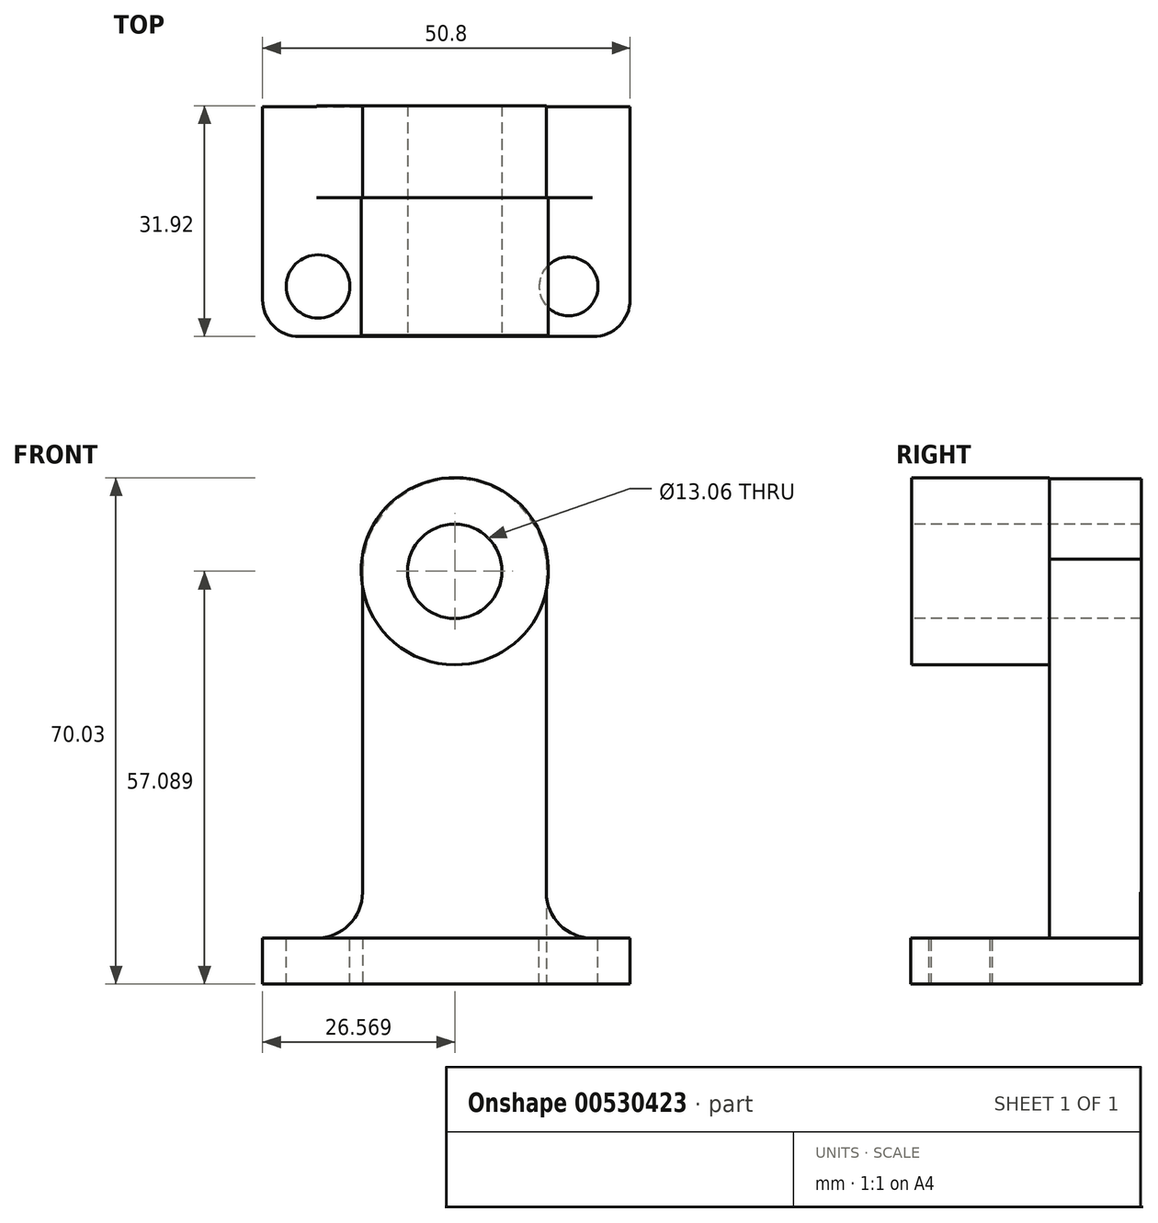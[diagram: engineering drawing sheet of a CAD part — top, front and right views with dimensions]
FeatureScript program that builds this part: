
annotation { "Feature Type Name" : "Feature", "Feature Type Description" : "" }
export const myFeature = defineFeature(function(context is Context, id is Id, definition is map)
    precondition{}
    {
        {
            var Q0;
            Q0=qCreatedBy(makeId("Front.planeOp"),FACE);
            var sketch = newSketch(context, id + "F0", { "sketchPlane" : qUnion([Q0])});
            skLineSegment(sketch, "E0", {"start": v(-46.82, 69.85) * mm, "end": v(-46.82, 0) * mm});
            skLineSegment(sketch, "E1", {"start": v(-46.82, 69.85) * mm, "end": v(-21.42, 69.85) * mm});
            skLineSegment(sketch, "E2", {"start": v(-21.42, 69.85) * mm, "end": v(-21.42, 0) * mm});
            skLineSegment(sketch, "E3", {"start": v(-46.82, 0) * mm, "end": v(-21.42, 0) * mm});
            skSolve(sketch);
        }
        {
            var Q0;
            Q0 = qSketchRegion(id + "F0", true);
            extrude(context, id + "F1", {"entities" : qUnion([Q0]), "depth" : 12.7 * mm, "offsetDistance" : 25.4 * mm});
        }
        {
            var Q0;
            Q0=makeQuery(id+"F1.opExtrude","CAP_FACE",FACE,{"disambiguationData":[OSD([sQuery(id+"F0.wireOp",EDGE,"E0"),sQuery(id+"F0.wireOp",EDGE,"E1"),sQuery(id+"F0.wireOp",EDGE,"E2"),sQuery(id+"F0.wireOp",EDGE,"E3")])],"isStart":false});
            var sketch = newSketch(context, id + "F2", { "sketchPlane" : qUnion([Q0])});
            skArc(sketch, "E4", {"start": v(-21.42, 55.38) * mm, "mid": v(-33.17, 69.82) * mm, "end": v(-46.82, 57.16) * mm});
            skSolve(sketch);
        }
        {
            var Q0;
            {var subQ5=makeQuery(id+"F1.opExtrude","CAP_EDGE",EDGE,{"disambiguationData":[OSD([sQuery(id+"F0.wireOp",EDGE,"E1")])],"isStart":false});Q0=makeQuery(id+"F2.imprint","IMPRINT",FACE,{"disambiguationData":[TD([[makeQuery(id+"F2.imprint","IMPRINT",EDGE,{"derivedFrom":subQ5}),-1.0]])]});}
            extrude(context, id + "F3", {"entities" : qUnion([Q0]), "operationType" : NewBodyOperationType.REMOVE, "endBound" : BoundingType.THROUGH_ALL, "oppositeDirection" : true, "depth" : 25.4 * mm, "offsetDistance" : 25.4 * mm});
        }
        {
            var Q0;
            Q0=makeQuery(id+"F1.opExtrude","CAP_FACE",FACE,{"disambiguationData":[OSD([sQuery(id+"F0.wireOp",EDGE,"E0"),sQuery(id+"F0.wireOp",EDGE,"E1"),sQuery(id+"F0.wireOp",EDGE,"E2"),sQuery(id+"F0.wireOp",EDGE,"E3")])],"isStart":false});
            var sketch = newSketch(context, id + "F4", { "sketchPlane" : qUnion([Q0])});
            skCircle(sketch, "E5", {"center": v(-34.06, 57.09) * mm, "radius": 12.94 * mm});
            skSolve(sketch);
        }
        {
            var Q0;
            Q0=makeQuery(id+"F4.imprint","IMPRINT",FACE,{"disambiguationData":[TD([[makeQuery(id+"F4.imprint","IMPRINT",EDGE,{"derivedFrom":sQuery(id+"F4.wireOp",EDGE,"E5")}),1.0]])]});
            extrude(context, id + "F5", {"entities" : qUnion([Q0]), "operationType" : NewBodyOperationType.ADD, "depth" : 19.05 * mm, "offsetDistance" : 25.4 * mm});
        }
        {
            var Q0;
            Q0=makeQuery(id+"F5.opExtrude","CAP_FACE",FACE,{"disambiguationData":[OSD([sQuery(id+"F4.wireOp",EDGE,"E5")])],"isStart":false});
            var sketch = newSketch(context, id + "F6", { "sketchPlane" : qUnion([Q0])});
            skCircle(sketch, "E6", {"center": v(-34.06, 57.09) * mm, "radius": 6.53 * mm});
            skSolve(sketch);
        }
        {
            var Q0;
            Q0=makeQuery(id+"F6.imprint","IMPRINT",FACE,{"disambiguationData":[TD([[makeQuery(id+"F6.imprint","IMPRINT",EDGE,{"derivedFrom":sQuery(id+"F6.wireOp",EDGE,"E6")}),1.0]])]});
            extrude(context, id + "F7", {"entities" : qUnion([Q0]), "operationType" : NewBodyOperationType.REMOVE, "endBound" : BoundingType.THROUGH_ALL, "oppositeDirection" : true, "depth" : 25.4 * mm, "offsetDistance" : 25.4 * mm});
        }
        {
            var Q0;
            Q0=qCreatedBy(makeId("Top.planeOp"),FACE);
            var sketch = newSketch(context, id + "F8", { "sketchPlane" : qUnion([Q0])});
            skLineSegment(sketch, "E7.bottom", {"start": v(-60.63, -0.17) * mm, "end": v(-9.83, -0.17) * mm});
            skLineSegment(sketch, "E7.top", {"start": v(-60.63, -31.92) * mm, "end": v(-9.83, -31.92) * mm});
            skLineSegment(sketch, "E7.left", {"start": v(-60.63, -0.17) * mm, "end": v(-60.63, -31.92) * mm});
            skLineSegment(sketch, "E7.right", {"start": v(-9.83, -0.17) * mm, "end": v(-9.83, -31.92) * mm});
            skSolve(sketch);
        }
        {
            var Q0;
            Q0=makeQuery(id+"F8.imprint","IMPRINT",FACE,{"disambiguationData":[TD([[makeQuery(id+"F8.imprint","IMPRINT",EDGE,{"derivedFrom":sQuery(id+"F8.wireOp",EDGE,"E7.bottom")}),-1.0]])]});
            extrude(context, id + "F9", {"entities" : qUnion([Q0]), "operationType" : NewBodyOperationType.ADD, "depth" : 6.35 * mm, "offsetDistance" : 25.4 * mm});
        }
        {
            var Q0;
            Q0=makeQuery(id+"F9.opExtrude","CAP_FACE",FACE,{"disambiguationData":[OSD([sQuery(id+"F8.wireOp",EDGE,"E7.bottom"),sQuery(id+"F8.wireOp",EDGE,"E7.top"),sQuery(id+"F8.wireOp",EDGE,"E7.left"),sQuery(id+"F8.wireOp",EDGE,"E7.right")])],"isStart":false});
            var sketch = newSketch(context, id + "F10", { "sketchPlane" : qUnion([Q0])});
            skCircle(sketch, "E8", {"center": v(-18.33, -24.99) * mm, "radius": 4.06 * mm});
            skCircle(sketch, "E9", {"center": v(-52.95, -24.99) * mm, "radius": 4.38 * mm});
            skSolve(sketch);
        }
        {
            var Q0;
            Q0=makeQuery(id+"F10.imprint","IMPRINT",FACE,{"disambiguationData":[TD([[makeQuery(id+"F10.imprint","IMPRINT",EDGE,{"derivedFrom":sQuery(id+"F10.wireOp",EDGE,"fPW7hecr-RpFH-Evfj-kExd-6QSjVOmFYihe")}),1.0]])]});
            var Q1;
            Q1=makeQuery(id+"F10.imprint","IMPRINT",FACE,{"disambiguationData":[TD([[makeQuery(id+"F10.imprint","IMPRINT",EDGE,{"derivedFrom":sQuery(id+"F10.wireOp",EDGE,"HLfQN0Yi-punc-iS16-G6WA-ixTniyIDgVXK")}),1.0]])]});
            var Q2;
            Q2=makeQuery(id+"F10.imprint","IMPRINT",FACE,{"disambiguationData":[TD([[makeQuery(id+"F10.imprint","IMPRINT",EDGE,{"derivedFrom":sQuery(id+"F10.wireOp",EDGE,"E9")}),1.0]])]});
            var Q3;
            Q3=makeQuery(id+"F10.imprint","IMPRINT",FACE,{"disambiguationData":[TD([[makeQuery(id+"F10.imprint","IMPRINT",EDGE,{"derivedFrom":sQuery(id+"F10.wireOp",EDGE,"E8")}),1.0]])]});
            extrude(context, id + "F11", {"entities" : qUnion([Q0, Q1, Q2, Q3]), "operationType" : NewBodyOperationType.REMOVE, "oppositeDirection" : true, "depth" : 25.4 * mm, "offsetDistance" : 25.4 * mm});
        }
        {
            var Q0;
            Q0=qCreatedBy(makeId("Front.planeOp"),FACE);
            var sketch = newSketch(context, id + "F12", { "sketchPlane" : qUnion([Q0])});
            skLineSegment(sketch, "E10.bottom", {"start": v(-47.13, 19.55) * mm, "end": v(-59.83, 19.55) * mm});
            skLineSegment(sketch, "E10.top", {"start": v(-47.13, 6.85) * mm, "end": v(-59.83, 6.85) * mm});
            skLineSegment(sketch, "E10.left", {"start": v(-47.13, 19.55) * mm, "end": v(-47.13, 6.85) * mm});
            skLineSegment(sketch, "E10.right", {"start": v(-59.83, 19.55) * mm, "end": v(-59.83, 6.85) * mm});
            skLineSegment(sketch, "E11.bottom", {"start": v(-21.07, 19.06) * mm, "end": v(-8.37, 19.06) * mm});
            skLineSegment(sketch, "E11.top", {"start": v(-21.07, 6.36) * mm, "end": v(-8.37, 6.36) * mm});
            skLineSegment(sketch, "E11.left", {"start": v(-21.07, 19.06) * mm, "end": v(-21.07, 6.36) * mm});
            skLineSegment(sketch, "E11.right", {"start": v(-8.37, 19.06) * mm, "end": v(-8.37, 6.36) * mm});
            skCircle(sketch, "E12", {"center": v(-53.48, 13.2) * mm, "radius": 6.35 * mm});
            skCircle(sketch, "E13", {"center": v(-14.9, 12.53) * mm, "radius": 6.17 * mm});
            skSolve(sketch);
        }
        {
            var Q0;
            {var subQ0=sQuery(id+"F12.wireOp",EDGE,"E12");var subQ1=makeQuery(id+"F12.imprint","INTERSECT",VERTEX,{"derivedFrom":[sQuery(id+"F12.wireOp",EDGE,"E10.bottom"),subQ0]});Q0=makeQuery(id+"F12.imprint","IMPRINT",FACE,{"disambiguationData":[TD([[makeQuery(id+"F12.imprint","IMPRINT",EDGE,{"disambiguationData":[TD([[subQ1,1.0]])],"derivedFrom":subQ0}),1.0]])]});}
            var Q1;
            {var subQ0=sQuery(id+"F12.wireOp",EDGE,"E10.right");var subQ1=sQuery(id+"F12.wireOp",EDGE,"E10.bottom");var subQ2=makeQuery(id+"F12.imprint","INTERSECT",VERTEX,{"derivedFrom":[subQ1,subQ0]});Q1=makeQuery(id+"F12.imprint","IMPRINT",FACE,{"disambiguationData":[TD([[makeQuery(id+"F12.imprint","IMPRINT",EDGE,{"disambiguationData":[TD([[subQ2,1.0]])],"derivedFrom":subQ1}),1.0]])]});}
            var Q2;
            {var subQ0=sQuery(id+"F12.wireOp",EDGE,"E10.right");var subQ1=sQuery(id+"F12.wireOp",EDGE,"E10.top");var subQ2=makeQuery(id+"F12.imprint","INTERSECT",VERTEX,{"derivedFrom":[subQ1,subQ0]});Q2=makeQuery(id+"F12.imprint","IMPRINT",FACE,{"disambiguationData":[TD([[makeQuery(id+"F12.imprint","IMPRINT",EDGE,{"disambiguationData":[TD([[subQ2,1.0]])],"derivedFrom":subQ1}),-1.0]])]});}
            var Q3;
            {var subQ0=sQuery(id+"F12.wireOp",EDGE,"E10.left");var subQ1=sQuery(id+"F12.wireOp",EDGE,"E10.bottom");var subQ2=makeQuery(id+"F12.imprint","INTERSECT",VERTEX,{"derivedFrom":[subQ1,subQ0]});Q3=makeQuery(id+"F12.imprint","IMPRINT",FACE,{"disambiguationData":[TD([[makeQuery(id+"F12.imprint","IMPRINT",EDGE,{"disambiguationData":[TD([[subQ2,-1.0]])],"derivedFrom":subQ1}),1.0]])]});}
            var Q4;
            {var subQ0=sQuery(id+"F12.wireOp",EDGE,"E13");var subQ1=makeQuery(id+"F12.imprint","INTERSECT",VERTEX,{"derivedFrom":[sQuery(id+"F12.wireOp",EDGE,"E11.top"),subQ0]});Q4=makeQuery(id+"F12.imprint","IMPRINT",FACE,{"disambiguationData":[TD([[makeQuery(id+"F12.imprint","IMPRINT",EDGE,{"disambiguationData":[TD([[subQ1,1.0]])],"derivedFrom":subQ0}),1.0]])]});}
            extrude(context, id + "F13", {"entities" : qUnion([Q0, Q1, Q2, Q3, Q4]), "operationType" : NewBodyOperationType.REMOVE, "endBound" : BoundingType.THROUGH_ALL, "oppositeDirection" : true, "depth" : 25.4 * mm, "offsetDistance" : 25.4 * mm});
        }
        {
            var Q0;
            Q0=makeQuery(id+"F9.opExtrude","SWEPT_EDGE",EDGE,{"disambiguationData":[OSD([sQuery(id+"F8.wireOp",EDGE,"E7.top"),sQuery(id+"F8.wireOp",EDGE,"E7.right")])]});
            var Q1;
            Q1=makeQuery(id+"F9.opExtrude","SWEPT_EDGE",EDGE,{"disambiguationData":[OSD([sQuery(id+"F8.wireOp",EDGE,"E7.top"),sQuery(id+"F8.wireOp",EDGE,"E7.left")])]});
            fillet(context, id + "F14", {"entities" : qUnion([Q0, Q1]), "radius" : 5.08 * mm, "tangentPropagation" : true, "allowEdgeOverflow" : false});
        }
        {
            var Q0;
            Q0=makeQuery(id+"F1.opExtrude","SWEPT_FACE",FACE,{"disambiguationData":[OSD([sQuery(id+"F0.wireOp",EDGE,"E2")])]});
            var sketch = newSketch(context, id + "F15", { "sketchPlane" : qUnion([Q0])});
            skLineSegment(sketch, "E14.bottom", {"start": v(-12.7, 15.74) * mm, "end": v(-0.17, 15.74) * mm});
            skLineSegment(sketch, "E14.top", {"start": v(-12.7, 6.35) * mm, "end": v(-0.17, 6.35) * mm});
            skLineSegment(sketch, "E14.left", {"start": v(-12.7, 15.74) * mm, "end": v(-12.7, 6.35) * mm});
            skLineSegment(sketch, "E14.right", {"start": v(-0.17, 15.74) * mm, "end": v(-0.17, 6.35) * mm});
            skSolve(sketch);
        }
        {
            var Q0;
            Q0=makeQuery(id+"F15.imprint","IMPRINT",FACE,{"disambiguationData":[TD([[makeQuery(id+"F15.imprint","IMPRINT",EDGE,{"derivedFrom":sQuery(id+"F15.wireOp",EDGE,"E14.bottom")}),-1.0]])]});
            extrude(context, id + "F16", {"entities" : qUnion([Q0]), "operationType" : NewBodyOperationType.ADD, "depth" : 12.7 * mm, "offsetDistance" : 25.4 * mm});
        }
        {
            var Q0;
            Q0=makeQuery(id+"F16.boolean.opBoolean","MERGE",FACE,{"derivedFrom":[makeQuery(id+"F1.opExtrude","CAP_FACE",FACE,{"disambiguationData":[OSD([sQuery(id+"F0.wireOp",EDGE,"E0"),sQuery(id+"F0.wireOp",EDGE,"E1"),sQuery(id+"F0.wireOp",EDGE,"E2"),sQuery(id+"F0.wireOp",EDGE,"E3")])],"isStart":false}),makeQuery(id+"F16.opExtrude","SWEPT_FACE",FACE,{"disambiguationData":[OSD([sQuery(id+"F15.wireOp",EDGE,"E14.left")])]})]});
            var sketch = newSketch(context, id + "F17", { "sketchPlane" : qUnion([Q0])});
            skLineSegment(sketch, "E15", {"start": v(-21.42, 15.74) * mm, "end": v(-21.42, 6.35) * mm});
            skLineSegment(sketch, "E16", {"start": v(-8.72, 15.74) * mm, "end": v(-8.72, 6.35) * mm});
            skCircle(sketch, "E17", {"center": v(-15.07, 12.7) * mm, "radius": 6.35 * mm});
            skSolve(sketch);
        }
        {
            var Q0;
            {var subQ0=sQuery(id+"F17.wireOp",EDGE,"E17");var subQ1=makeQuery(id+"F17.imprint","INTERSECT",VERTEX,{"derivedFrom":[sQuery(id+"F17.wireOp",EDGE,"E16"),subQ0]});Q0=makeQuery(id+"F17.imprint","IMPRINT",FACE,{"disambiguationData":[TD([[makeQuery(id+"F17.imprint","IMPRINT",EDGE,{"disambiguationData":[TD([[subQ1,-1.0]])],"derivedFrom":subQ0}),1.0]])]});}
            var Q1;
            {var subQ0=sQuery(id+"F17.wireOp",EDGE,"E17");var subQ1=makeQuery(id+"F16.opExtrude","SWEPT_EDGE",EDGE,{"disambiguationData":[OSD([sQuery(id+"F0.wireOp",EDGE,"E2"),sQuery(id+"F15.wireOp",EDGE,"E14.bottom"),sQuery(id+"F15.wireOp",EDGE,"E14.left")])]});var subQ2=makeQuery(id+"F17.imprint","INTERSECT",VERTEX,{"disambiguationData":[OD(0.0)],"derivedFrom":[subQ1,subQ0]});Q1=makeQuery(id+"F17.imprint","IMPRINT",FACE,{"disambiguationData":[TD([[makeQuery(id+"F17.imprint","IMPRINT",EDGE,{"disambiguationData":[TD([[subQ2,-1.0]])],"derivedFrom":subQ0}),1.0]])]});}
            var Q2;
            {var subQ1=makeQuery(id+"F16.opExtrude","SWEPT_EDGE",EDGE,{"disambiguationData":[OSD([sQuery(id+"F15.wireOp",EDGE,"E14.top"),sQuery(id+"F15.wireOp",EDGE,"E14.left")])]});var subQ2=makeQuery(id+"F16.boolean.opBoolean","SPLIT",EDGE,{"derivedFrom":subQ1});Q2=makeQuery(id+"F17.imprint","IMPRINT",FACE,{"disambiguationData":[TD([[makeQuery(id+"F17.imprint","IMPRINT",EDGE,{"derivedFrom":subQ2}),-1.0]])]});}
            var Q3;
            {var subQ0=sQuery(id+"F17.wireOp",EDGE,"E16");var subQ3=sQuery(id+"F17.wireOp",EDGE,"E17");var subQ4=makeQuery(id+"F17.imprint","INTERSECT",VERTEX,{"derivedFrom":[subQ0,subQ3]});Q3=makeQuery(id+"F17.imprint","IMPRINT",FACE,{"disambiguationData":[TD([[makeQuery(id+"F17.imprint","IMPRINT",EDGE,{"disambiguationData":[TD([[subQ4,1.0]])],"derivedFrom":subQ0}),-1.0]])]});}
            extrude(context, id + "F18", {"entities" : qUnion([Q0, Q1, Q2, Q3]), "operationType" : NewBodyOperationType.REMOVE, "oppositeDirection" : true, "depth" : 25.4 * mm, "offsetDistance" : 25.4 * mm});
        }
        {
            var Q0;
            Q0=makeQuery(id+"F1.opExtrude","SWEPT_FACE",FACE,{"disambiguationData":[OSD([sQuery(id+"F0.wireOp",EDGE,"E0")])]});
            var sketch = newSketch(context, id + "F19", { "sketchPlane" : qUnion([Q0])});
            skLineSegment(sketch, "E18.bottom", {"start": v(0, 16.45) * mm, "end": v(12.7, 16.45) * mm});
            skLineSegment(sketch, "E18.top", {"start": v(0, 6.35) * mm, "end": v(12.7, 6.35) * mm});
            skLineSegment(sketch, "E18.left", {"start": v(0, 16.45) * mm, "end": v(0, 6.35) * mm});
            skLineSegment(sketch, "E18.right", {"start": v(12.7, 16.45) * mm, "end": v(12.7, 6.35) * mm});
            skSolve(sketch);
        }
        {
            var Q0;
            Q0=makeQuery(id+"F19.imprint","IMPRINT",FACE,{"disambiguationData":[TD([[makeQuery(id+"F19.imprint","IMPRINT",EDGE,{"derivedFrom":sQuery(id+"F19.wireOp",EDGE,"E18.bottom")}),-1.0]])]});
            extrude(context, id + "F20", {"entities" : qUnion([Q0]), "operationType" : NewBodyOperationType.ADD, "depth" : 12.7 * mm, "offsetDistance" : 25.4 * mm});
        }
        {
            var Q0;
            Q0=makeQuery(id+"F20.boolean.opBoolean","MERGE",FACE,{"derivedFrom":[makeQuery(id+"F16.boolean.opBoolean","MERGE",FACE,{"derivedFrom":[makeQuery(id+"F1.opExtrude","CAP_FACE",FACE,{"disambiguationData":[OSD([sQuery(id+"F0.wireOp",EDGE,"E0"),sQuery(id+"F0.wireOp",EDGE,"E1"),sQuery(id+"F0.wireOp",EDGE,"E2"),sQuery(id+"F0.wireOp",EDGE,"E3")])],"isStart":false}),makeQuery(id+"F16.opExtrude","SWEPT_FACE",FACE,{"disambiguationData":[OSD([sQuery(id+"F15.wireOp",EDGE,"E14.left")])]})]}),makeQuery(id+"F20.opExtrude","SWEPT_FACE",FACE,{"disambiguationData":[OSD([sQuery(id+"F19.wireOp",EDGE,"E18.right")])]})]});
            var sketch = newSketch(context, id + "F21", { "sketchPlane" : qUnion([Q0])});
            skLineSegment(sketch, "E19", {"start": v(-46.82, 16.45) * mm, "end": v(-46.82, 6.35) * mm});
            skLineSegment(sketch, "E20", {"start": v(-21.42, 26.05) * mm, "end": v(-21.42, 6.35) * mm});
            skCircle(sketch, "E21", {"center": v(-53.17, 12.7) * mm, "radius": 6.35 * mm});
            skSolve(sketch);
        }
        {
            var Q0;
            {var subQ0=sQuery(id+"F21.wireOp",EDGE,"E21");var subQ1=sQuery(id+"F19.wireOp",EDGE,"E18.right");var subQ2=makeQuery(id+"F20.opExtrude","CAP_EDGE",EDGE,{"disambiguationData":[OSD([subQ1])],"isStart":false});var subQ3=makeQuery(id+"F21.imprint","INTERSECT",VERTEX,{"derivedFrom":[subQ2,subQ0]});Q0=makeQuery(id+"F21.imprint","IMPRINT",FACE,{"disambiguationData":[TD([[makeQuery(id+"F21.imprint","IMPRINT",EDGE,{"disambiguationData":[TD([[subQ3,-1.0]])],"derivedFrom":subQ0}),-1.0]])]});}
            var Q1;
            {var subQ1=makeQuery(id+"F16.opExtrude","SWEPT_EDGE",EDGE,{"disambiguationData":[OSD([sQuery(id+"F0.wireOp",EDGE,"E2"),sQuery(id+"F15.wireOp",EDGE,"E14.bottom"),sQuery(id+"F15.wireOp",EDGE,"E14.left")])]});Q1=makeQuery(id+"F21.imprint","IMPRINT",FACE,{"disambiguationData":[TD([[makeQuery(id+"F21.imprint","IMPRINT",EDGE,{"derivedFrom":subQ1}),1.0]])]});}
            var Q2;
            {var subQ0=sQuery(id+"F21.wireOp",EDGE,"E21");var subQ1=sQuery(id+"F19.wireOp",EDGE,"E18.right");var subQ4=makeQuery(id+"F20.opExtrude","CAP_EDGE",EDGE,{"disambiguationData":[OSD([subQ1])],"isStart":false});var subQ5=makeQuery(id+"F21.imprint","INTERSECT",VERTEX,{"derivedFrom":[subQ4,subQ0]});Q2=makeQuery(id+"F21.imprint","IMPRINT",FACE,{"disambiguationData":[TD([[makeQuery(id+"F21.imprint","IMPRINT",EDGE,{"disambiguationData":[TD([[subQ5,1.0]])],"derivedFrom":subQ0}),-1.0]])]});}
            var Q3;
            {var subQ0=sQuery(id+"F21.wireOp",EDGE,"E21");var subQ1=makeQuery(id+"F20.opExtrude","SWEPT_EDGE",EDGE,{"disambiguationData":[OSD([sQuery(id+"F0.wireOp",EDGE,"E0"),sQuery(id+"F19.wireOp",EDGE,"E18.bottom"),sQuery(id+"F19.wireOp",EDGE,"E18.right")])]});var subQ2=makeQuery(id+"F21.imprint","INTERSECT",VERTEX,{"disambiguationData":[OD(0.0)],"derivedFrom":[subQ1,subQ0]});Q3=makeQuery(id+"F21.imprint","IMPRINT",FACE,{"disambiguationData":[TD([[makeQuery(id+"F21.imprint","IMPRINT",EDGE,{"disambiguationData":[TD([[subQ2,-1.0]])],"derivedFrom":subQ0}),1.0]])]});}
            var Q4;
            {var subQ0=sQuery(id+"F21.wireOp",EDGE,"E21");var subQ1=makeQuery(id+"F21.imprint","INTERSECT",VERTEX,{"derivedFrom":[sQuery(id+"F21.wireOp",EDGE,"E19"),subQ0]});Q4=makeQuery(id+"F21.imprint","IMPRINT",FACE,{"disambiguationData":[TD([[makeQuery(id+"F21.imprint","IMPRINT",EDGE,{"disambiguationData":[TD([[subQ1,-1.0]])],"derivedFrom":subQ0}),1.0]])]});}
            extrude(context, id + "F22", {"entities" : qUnion([Q0, Q1, Q2, Q3, Q4]), "operationType" : NewBodyOperationType.REMOVE, "oppositeDirection" : true, "depth" : 25.4 * mm, "offsetDistance" : 25.4 * mm});
        }
        {
            var Q0;
            Q0=makeQuery(id+"F20.boolean.opBoolean","MERGE",FACE,{"derivedFrom":[makeQuery(id+"F16.boolean.opBoolean","MERGE",FACE,{"derivedFrom":[makeQuery(id+"F1.opExtrude","CAP_FACE",FACE,{"disambiguationData":[OSD([sQuery(id+"F0.wireOp",EDGE,"E0"),sQuery(id+"F0.wireOp",EDGE,"E1"),sQuery(id+"F0.wireOp",EDGE,"E2"),sQuery(id+"F0.wireOp",EDGE,"E3")])],"isStart":false}),makeQuery(id+"F16.opExtrude","SWEPT_FACE",FACE,{"disambiguationData":[OSD([sQuery(id+"F15.wireOp",EDGE,"E14.left")])]})]}),makeQuery(id+"F20.opExtrude","SWEPT_FACE",FACE,{"disambiguationData":[OSD([sQuery(id+"F19.wireOp",EDGE,"E18.right")])]})]});
            var sketch = newSketch(context, id + "F23", { "sketchPlane" : qUnion([Q0])});
            skLineSegment(sketch, "E22", {"start": v(-46.82, 27.47) * mm, "end": v(-46.82, 6.35) * mm});
            skSolve(sketch);
        }
        {
            var Q0;
            {var subQ1=makeQuery(id+"F20.opExtrude","SWEPT_EDGE",EDGE,{"disambiguationData":[OSD([sQuery(id+"F0.wireOp",EDGE,"E0"),sQuery(id+"F19.wireOp",EDGE,"E18.bottom"),sQuery(id+"F19.wireOp",EDGE,"E18.right")])]});Q0=makeQuery(id+"F23.imprint","IMPRINT",FACE,{"disambiguationData":[TD([[makeQuery(id+"F23.imprint","IMPRINT",EDGE,{"derivedFrom":subQ1}),-1.0]])]});}
            extrude(context, id + "F24", {"entities" : qUnion([Q0]), "operationType" : NewBodyOperationType.REMOVE, "oppositeDirection" : true, "depth" : 25.4 * mm, "offsetDistance" : 25.4 * mm});
        }
    });
